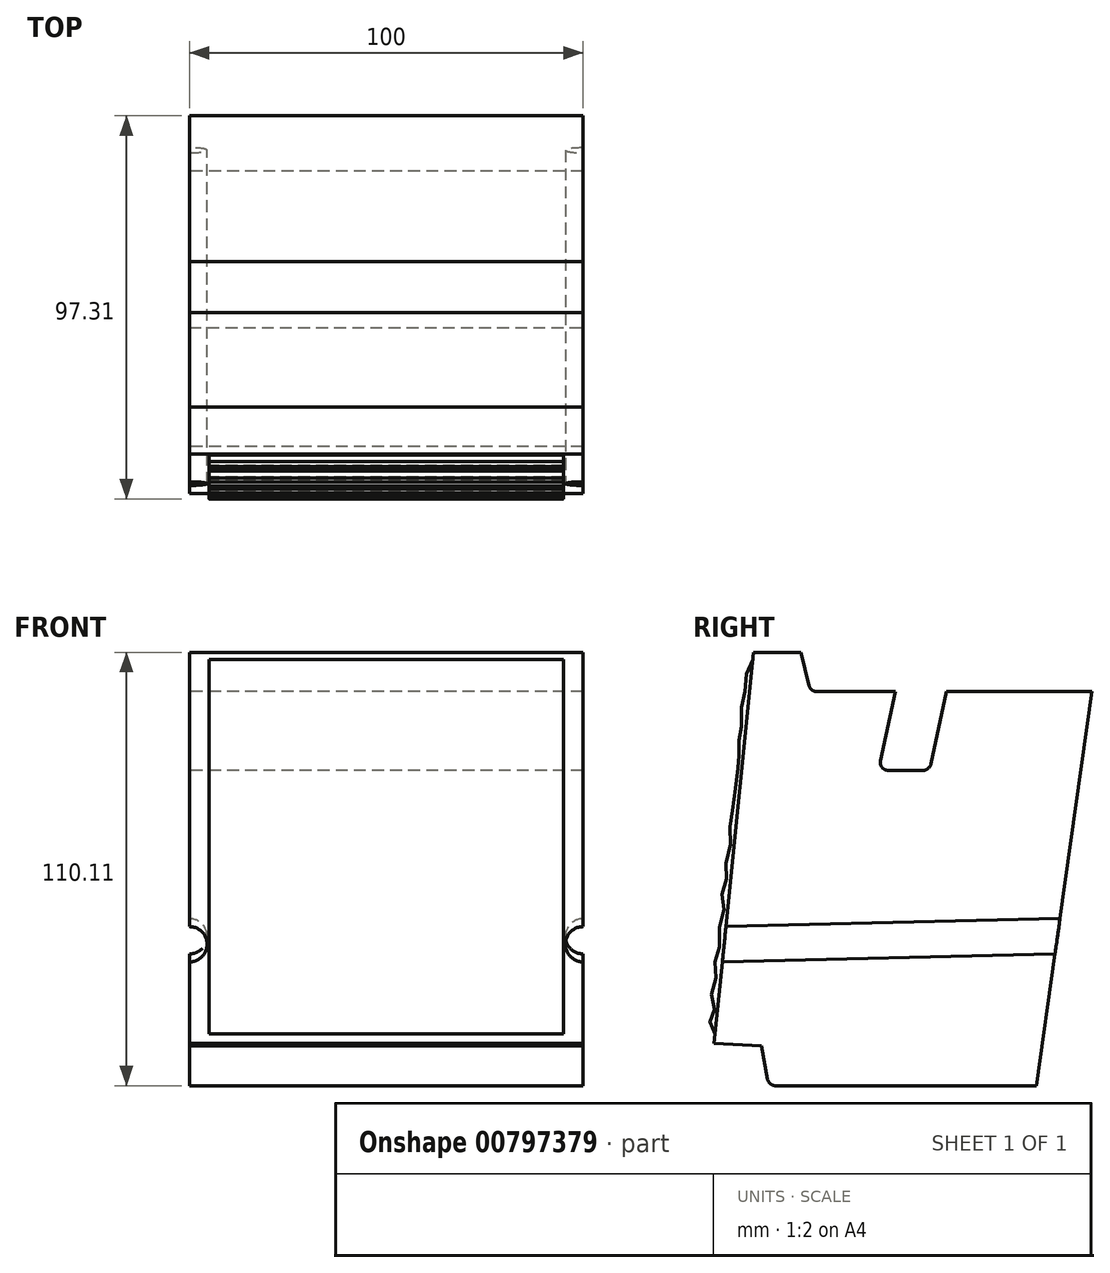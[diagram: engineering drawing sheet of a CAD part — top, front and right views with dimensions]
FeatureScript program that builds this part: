
annotation { "Feature Type Name" : "Feature", "Feature Type Description" : "" }
export const myFeature = defineFeature(function(context is Context, id is Id, definition is map)
    precondition{}
    {
        {
            var Q0;
            Q0=qCreatedBy(makeId("Right.planeOp"),FACE);
            var sketch = newSketch(context, id + "F0", { "sketchPlane" : qUnion([Q0])});
            skLineSegment(sketch, "E0", {"start": v(0, 0) * mm, "end": v(68, 0) * mm});
            skLineSegment(sketch, "E1", {"start": v(68, 0) * mm, "end": v(82.12, 100.1) * mm});
            skLineSegment(sketch, "E2", {"start": v(82.12, 100.1) * mm, "end": v(45.12, 100.1) * mm});
            skLineSegment(sketch, "E3", {"start": v(45.12, 100.1) * mm, "end": v(40.84, 80.1) * mm});
            skLineSegment(sketch, "E4", {"start": v(40.84, 80.1) * mm, "end": v(27.84, 80.1) * mm});
            skLineSegment(sketch, "E5", {"start": v(27.84, 80.1) * mm, "end": v(32.12, 100.1) * mm});
            skLineSegment(sketch, "E6", {"start": v(32.12, 100.1) * mm, "end": v(10.63, 100.1) * mm});
            skLineSegment(sketch, "E7", {"start": v(10.63, 100.1) * mm, "end": v(8.12, 110.1) * mm});
            skLineSegment(sketch, "E8", {"start": v(8.12, 110.1) * mm, "end": v(-3.88, 110.1) * mm});
            skLineSegment(sketch, "E9", {"start": v(-3.88, 110.1) * mm, "end": v(-13.88, 10.7) * mm});
            skLineSegment(sketch, "E10", {"start": v(-13.88, 10.7) * mm, "end": v(-1.88, 10.1) * mm});
            skLineSegment(sketch, "E11", {"start": v(-1.88, 10.1) * mm, "end": v(0, 0) * mm});
            skSolve(sketch);
        }
        {
            var Q0;
            Q0=qSketchRegion(id+"F0",true);
            extrude(context, id + "F1", {"entities" : qUnion([Q0]), "depth" : 100 * mm, "offsetDistance" : 25 * mm});
        }
        {
            var Q0;
            Q0=makeQuery(id+"F1.opExtrude","SWEPT_EDGE",EDGE,{"disambiguationData":[OSD([sQuery(id+"F0.wireOp",EDGE,"E6"),sQuery(id+"F0.wireOp",EDGE,"E7")])]});
            var Q1;
            Q1=makeQuery(id+"F1.opExtrude","SWEPT_EDGE",EDGE,{"disambiguationData":[OSD([sQuery(id+"F0.wireOp",EDGE,"E4"),sQuery(id+"F0.wireOp",EDGE,"E5")])]});
            var Q2;
            Q2=makeQuery(id+"F1.opExtrude","SWEPT_EDGE",EDGE,{"disambiguationData":[OSD([sQuery(id+"F0.wireOp",EDGE,"E3"),sQuery(id+"F0.wireOp",EDGE,"E4")])]});
            var Q3;
            Q3=makeQuery(id+"F1.opExtrude","SWEPT_EDGE",EDGE,{"disambiguationData":[OSD([sQuery(id+"F0.wireOp",EDGE,"E0"),sQuery(id+"F0.wireOp",EDGE,"E11")])]});
            fillet(context, id + "F2", {"entities" : qUnion([Q0, Q1, Q2, Q3]), "radius" : 2 * mm, "tangentPropagation" : true, "allowEdgeOverflow" : false});
        }
        {
            var Q0;
            Q0=makeQuery(id+"F1.opExtrude","CAP_FACE",FACE,{"disambiguationData":[OSD([sQuery(id+"F0.wireOp",EDGE,"E0"),sQuery(id+"F0.wireOp",EDGE,"E1"),sQuery(id+"F0.wireOp",EDGE,"E2"),sQuery(id+"F0.wireOp",EDGE,"E3"),sQuery(id+"F0.wireOp",EDGE,"E4"),sQuery(id+"F0.wireOp",EDGE,"E5"),sQuery(id+"F0.wireOp",EDGE,"E6"),sQuery(id+"F0.wireOp",EDGE,"E7"),sQuery(id+"F0.wireOp",EDGE,"E8"),sQuery(id+"F0.wireOp",EDGE,"E9"),sQuery(id+"F0.wireOp",EDGE,"E10"),sQuery(id+"F0.wireOp",EDGE,"E11")])],"isStart":false});
            var sketch = newSketch(context, id + "F3", { "sketchPlane" : qUnion([Q0])});
            skLineSegment(sketch, "E12", {"start": v(-11.34, 35.93) * mm, "end": v(89.67, 38.34) * mm});
            skSolve(sketch);
        }
        {
            var Q0;
            Q0=makeQuery(id+"F1.opExtrude","SWEPT_FACE",FACE,{"disambiguationData":[OSD([sQuery(id+"F0.wireOp",EDGE,"E9")])]});
            var sketch = newSketch(context, id + "F4", { "sketchPlane" : qUnion([Q0])});
            skLineSegment(sketch, "E13.0", {"start": v(100, 34.62) * mm, "end": v(100, 47.13) * mm});
            skCircle(sketch, "E14", {"center": v(100, 34.62) * mm, "radius": 4.5 * mm});
            skSolve(sketch);
        }
        {
            var Q0;
            {var subQ0=sQuery(id+"F4.wireOp",EDGE,"E13.0");var subQ1=makeQuery(id+"F1.opExtrude","CAP_EDGE",EDGE,{"disambiguationData":[OSD([sQuery(id+"F0.wireOp",EDGE,"E9")])],"isStart":false});var subQ2=makeQuery(id+"F4.imprint","INTERSECT",VERTEX,{"disambiguationData":[OD(1.0)],"derivedFrom":[subQ1,subQ0]});Q0=makeQuery(id+"F4.imprint","IMPRINT",FACE,{"disambiguationData":[TD([[makeQuery(id+"F4.imprint","IMPRINT",EDGE,{"disambiguationData":[TD([[subQ2,1.0]])],"derivedFrom":subQ0}),-1.0]])]});}
            var Q1;
            Q1=sQuery(id+"F3.wireOp",EDGE,"E12");
            sweep(context, id + "F5", {"profiles" : qUnion([Q0]), "path" : qUnion([Q1])});
        }
        {
            var Q0;
            Q0=makeQuery(id+"F1.opExtrude","CAP_FACE",FACE,{"disambiguationData":[OSD([sQuery(id+"F0.wireOp",EDGE,"E0"),sQuery(id+"F0.wireOp",EDGE,"E1"),sQuery(id+"F0.wireOp",EDGE,"E2"),sQuery(id+"F0.wireOp",EDGE,"E3"),sQuery(id+"F0.wireOp",EDGE,"E4"),sQuery(id+"F0.wireOp",EDGE,"E5"),sQuery(id+"F0.wireOp",EDGE,"E6"),sQuery(id+"F0.wireOp",EDGE,"E7"),sQuery(id+"F0.wireOp",EDGE,"E8"),sQuery(id+"F0.wireOp",EDGE,"E9"),sQuery(id+"F0.wireOp",EDGE,"E10"),sQuery(id+"F0.wireOp",EDGE,"E11")])],"isStart":true});
            var Q1;
            {var subQ0=sQuery(id+"F0.wireOp",EDGE,"E9");var subQ1=sQuery(id+"F0.wireOp",EDGE,"E5");var subQ2=sQuery(id+"F0.wireOp",EDGE,"E4");var subQ3=sQuery(id+"F0.wireOp",EDGE,"E8");var subQ4=sQuery(id+"F0.wireOp",EDGE,"E3");var subQ5=sQuery(id+"F0.wireOp",EDGE,"E7");var subQ6=sQuery(id+"F0.wireOp",EDGE,"E6");var subQ7=sQuery(id+"F0.wireOp",EDGE,"E1");var subQ8=sQuery(id+"F0.wireOp",EDGE,"E2");Q1=makeQuery(id+"F5.boolean.opBoolean","SPLIT",FACE,{"disambiguationData":[TD([makeQuery(id+"F1.opExtrude","SWEPT_FACE",FACE,{"disambiguationData":[OSD([subQ8])]})])],"derivedFrom":makeQuery(id+"F1.opExtrude","CAP_FACE",FACE,{"disambiguationData":[OSD([sQuery(id+"F0.wireOp",EDGE,"E0"),subQ7,subQ8,subQ4,subQ2,subQ1,subQ6,subQ5,subQ3,subQ0,sQuery(id+"F0.wireOp",EDGE,"E10"),sQuery(id+"F0.wireOp",EDGE,"E11")])],"isStart":false})});}
            cPlane(context, id + "F6", {"entities" : qUnion([Q0, Q1]), "cplaneType" : CPlaneType.MID_PLANE, "offset" : 25 * mm, "width" : 150 * mm, "height" : 150 * mm});
        }
        {
            var Q0;
            Q0=makeQuery(id+"F5.opSweep","SWEPT_BODY",BODY,{"disambiguationData":[OSD([sQuery(id+"F0.wireOp",EDGE,"E9"),sQuery(id+"F3.wireOp",EDGE,"E12"),sQuery(id+"F4.wireOp",EDGE,"E13.0"),sQuery(id+"F4.wireOp",EDGE,"E14")])]});
            var Q1;
            Q1=qCreatedBy(id+"F6.planeOp",FACE);
            mirror(context, id + "F7", {"operationType" : NewBodyOperationType.REMOVE, "entities" : qUnion([Q0]), "mirrorPlane" : qUnion([Q1])});
        }
        {
            var Q0;
            Q0=makeQuery(id+"F5.opSweep","SWEPT_BODY",BODY,{"disambiguationData":[OSD([sQuery(id+"F0.wireOp",EDGE,"E9"),sQuery(id+"F3.wireOp",EDGE,"E12"),sQuery(id+"F4.wireOp",EDGE,"E13.0"),sQuery(id+"F4.wireOp",EDGE,"E14")])]});
            var Q1;
            Q1=makeQuery(id+"F1.opExtrude","SWEPT_BODY",BODY,{"disambiguationData":[OSD([sQuery(id+"F0.wireOp",EDGE,"E0"),sQuery(id+"F0.wireOp",EDGE,"E1"),sQuery(id+"F0.wireOp",EDGE,"E2"),sQuery(id+"F0.wireOp",EDGE,"E3"),sQuery(id+"F0.wireOp",EDGE,"E4"),sQuery(id+"F0.wireOp",EDGE,"E5"),sQuery(id+"F0.wireOp",EDGE,"E6"),sQuery(id+"F0.wireOp",EDGE,"E7"),sQuery(id+"F0.wireOp",EDGE,"E8"),sQuery(id+"F0.wireOp",EDGE,"E9"),sQuery(id+"F0.wireOp",EDGE,"E10"),sQuery(id+"F0.wireOp",EDGE,"E11")])]});
            booleanBodies(context, id + "F8", {"operationType" : BooleanOperationType.SUBTRACTION, "tools" : qUnion([Q0]), "targets" : qUnion([Q1])});
        }
        {
            var Q0;
            {var subQ0=sQuery(id+"F0.wireOp",EDGE,"E9");var subQ1=sQuery(id+"F0.wireOp",EDGE,"E5");var subQ2=sQuery(id+"F0.wireOp",EDGE,"E4");var subQ3=sQuery(id+"F0.wireOp",EDGE,"E8");var subQ4=sQuery(id+"F0.wireOp",EDGE,"E3");var subQ5=sQuery(id+"F0.wireOp",EDGE,"E7");var subQ6=sQuery(id+"F0.wireOp",EDGE,"E6");var subQ7=sQuery(id+"F0.wireOp",EDGE,"E1");var subQ8=sQuery(id+"F0.wireOp",EDGE,"E2");Q0=makeQuery(id+"F8.opBoolean","SPLIT",FACE,{"disambiguationData":[TD([makeQuery(id+"F1.opExtrude","SWEPT_FACE",FACE,{"disambiguationData":[OSD([subQ8])]})])],"derivedFrom":makeQuery(id+"F1.opExtrude","CAP_FACE",FACE,{"disambiguationData":[OSD([sQuery(id+"F0.wireOp",EDGE,"E0"),subQ7,subQ8,subQ4,subQ2,subQ1,subQ6,subQ5,subQ3,subQ0,sQuery(id+"F0.wireOp",EDGE,"E10"),sQuery(id+"F0.wireOp",EDGE,"E11")])],"isStart":false})});}
            cPlane(context, id + "F9", {"entities" : qUnion([Q0]), "cplaneType" : CPlaneType.OFFSET, "offset" : 5 * mm, "oppositeDirection" : true, "width" : 150 * mm, "height" : 150 * mm});
        }
        {
            var Q0;
            Q0=qCreatedBy(id+"F9.planeOp",FACE);
            var sketch = newSketch(context, id + "F10", { "sketchPlane" : qUnion([Q0])});
            skFitSpline(sketch, "E15", {"points": [v(-4.07, 108.22) * mm, v(-5.7, 105.52) * mm, v(-5.69, 104.27) * mm, v(-5.82, 100.86) * mm, v(-6.65, 98.2) * mm, v(-6.96, 95.64) * mm, v(-6.76, 92.01) * mm, v(-7.55, 89.48) * mm, v(-7.56, 87.88) * mm, v(-7.96, 85.6) * mm, v(-7.55, 83.57) * mm, v(-8.11, 81.77) * mm, v(-7.78, 80.25) * mm, v(-8.43, 76.1) * mm, v(-9.03, 70.81) * mm, v(-9.75, 68.08) * mm, v(-9.88, 65.4) * mm, v(-9.7, 63.32) * mm, v(-10.29, 58.24) * mm, v(-10.9, 56.09) * mm, v(-10.64, 53.21) * mm, v(-10.9, 52.07) * mm, v(-11.98, 49.13) * mm, v(-10.96, 46.6) * mm, v(-11.5, 44.38) * mm, v(-12.45, 41.3) * mm, v(-12.63, 37.63) * mm, v(-12.71, 34.27) * mm, v(-13.65, 32.06) * mm, v(-13.52, 29.52) * mm, v(-13.45, 27.18) * mm, v(-14.17, 24.78) * mm, v(-14.52, 21.82) * mm, v(-13.79, 19.82) * mm, v(-14.66, 17.74) * mm, v(-14.92, 16.6) * mm, v(-15.12, 14.53) * mm, v(-13.63, 13.18) * mm], "startDerivative": vector(-121.63, -96) * mm, "endDerivative": vector(79.77, -48.28) * mm});
            skLineSegment(sketch, "E16.0", {"start": v(-11.8, 31.45) * mm, "end": v(-13.88, 10.7) * mm});
            skLineSegment(sketch, "E17.0", {"start": v(-3.88, 110.1) * mm, "end": v(-10.9, 40.4) * mm});
            skLineSegment(sketch, "E18", {"start": v(-10.9, 40.4) * mm, "end": v(-11.8, 31.45) * mm});
            skSolve(sketch);
        }
        {
            var Q0;
            Q0=qSketchRegion(id+"F10",true);
            extrude(context, id + "F11", {"entities" : qUnion([Q0]), "operationType" : NewBodyOperationType.ADD, "oppositeDirection" : true, "depth" : 90 * mm, "offsetDistance" : 25 * mm});
        }
    });
